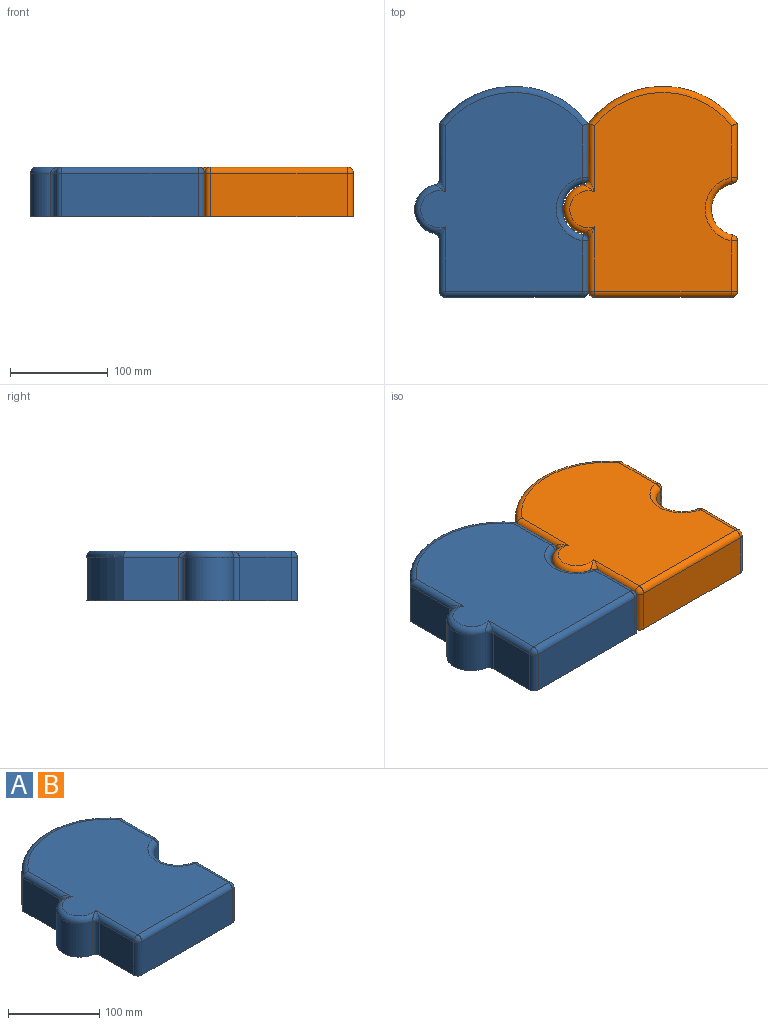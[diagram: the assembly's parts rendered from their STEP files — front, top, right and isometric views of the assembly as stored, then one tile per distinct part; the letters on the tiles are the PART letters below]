
ASSEMBLY  parts=2 mates=1
PART A: 30 faces, bbox 186.2x223.7x50.8 mm
  f0: plane 56.52x44.45mm, normal (-1,0,0), area 2512.4mm2, adj f7,f9,f11,f20
  f1: cylinder r=25.4mm len=49.77mm, axis (0,0,-1), area 3092.3mm2, adj f9,f13,f18,f20
  f2: plane 52.71x44.45mm, normal (-1,0,0), area 2343mm2, adj f9,f15,f18,f26
  f3: plane 139.7x44.45mm, normal (0,-1,0), area 6209.7mm2, adj f9,f17,f26,f28
  f4: plane 51.42x44.45mm, normal (1,0,0), area 2285.5mm2, adj f9,f16,f24,f28
  f5: cylinder r=26.67mm len=52.34mm, axis (0,0,-1), area 3265.5mm2, adj f9,f14,f22,f24
  f6: plane 55.23x44.45mm, normal (1,0,0), area 2454.8mm2, adj f7,f9,f12,f22
  f7: cylinder r=95.25mm len=152.4mm, axis (0,0,-1), area 7852.1mm2, adj f0,f6,f9,f10
  f8: plane 203.2x165.1mm, normal (0,0,1), area 26463.8mm2, adj f10,f11,f12,f13,f14,f15,f16,f17
  f9: plane 215.9x177.8mm, normal (0,0,-1), area 31033.5mm2, adj f0,f1,f2,f3,f4,f5,f6,f7
  f10: torus R=88.9mm, axis (0,0,1), area 1704.1mm2, adj f7,f8,f11,f12
  f11: cylinder r=6.35mm len=69.67mm, axis (0,1,0), area 599mm2, adj f0,f8,f10,f21
  f12: cylinder r=6.35mm len=55.23mm, axis (0,-1,0), area 543.1mm2, adj f6,f8,f10,f23
  f13: torus R=19.05mm, axis (0,0,1), area 698.3mm2, adj f1,f8,f19,f21
  f14: torus R=33.02mm, axis (0,0,1), area 796.2mm2, adj f5,f8,f23,f25
  f15: cylinder r=6.35mm len=65.86mm, axis (0,1,0), area 568.8mm2, adj f2,f8,f19,f27
  f16: cylinder r=6.35mm len=51.42mm, axis (0,-1,0), area 512.9mm2, adj f4,f8,f25,f29
  f17: cylinder r=6.35mm len=139.7mm, axis (-1,0,0), area 1393.4mm2, adj f3,f8,f27,f29
  f18: cylinder r=6.35mm len=44.45mm, axis (0,0,-1), area 386.5mm2, adj f1,f2,f9,f19
  f19: bspline ~13.16x11.44mm, area 70.6mm2, adj f13,f15,f18
  f20: cylinder r=6.35mm len=44.45mm, axis (0,0,-1), area 386.5mm2, adj f0,f1,f9,f21
  f21: bspline ~13.16x11.44mm, area 70.6mm2, adj f11,f13,f20
  f22: cylinder r=6.35mm len=44.45mm, axis (0,0,-1), area 388.7mm2, adj f5,f6,f9,f23
  f23: sphere r=6.35mm, area 55.5mm2, adj f12,f14,f22
  f24: cylinder r=6.35mm len=44.45mm, axis (0,0,-1), area 388.7mm2, adj f4,f5,f9,f25
  f25: sphere r=6.35mm, area 55.5mm2, adj f14,f16,f24
  f26: cylinder r=6.35mm len=44.45mm, axis (0,0,1), area 443.4mm2, adj f2,f3,f9,f27
  f27: sphere r=6.35mm, area 63.3mm2, adj f15,f17,f26
  f28: cylinder r=6.35mm len=44.45mm, axis (0,0,-1), area 443.4mm2, adj f3,f4,f9,f29
  f29: sphere r=6.35mm, area 63.3mm2, adj f16,f17,f28
PART B: same geometry as A
PLACE A t=(-25.4,0,0)mm
PLACE B t=(127,0,0)mm
MATE fastened B.f1 <-> A.f5  axis (0,0,1) through (50.8,90.17,50.8)mm
